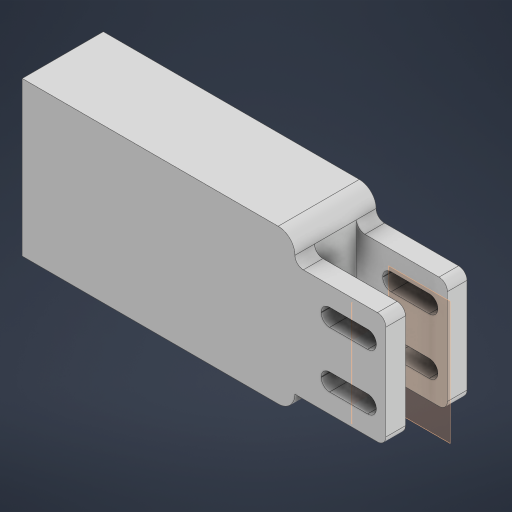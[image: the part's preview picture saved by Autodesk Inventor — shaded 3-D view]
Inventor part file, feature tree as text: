
AUTODESK INVENTOR PART (.ipt)
format: ipt  version: 2024 (Build 280153000, 153)  size: 675,840 bytes
history: native  units: mm
features: move_body x6, extrude x5, direct_edit x5, sketch x5, projected_geometry x5, fillet x4, plane x2, other x2, mirror x1, reference x1
ambient origin geometry x8: Origin, YZ Plane, XZ Plane, XY Plane, X Axis, Y Axis, Z Axis, Center Point
bodies: Solid1 (feature_tree)
feature tree (36):
  extrude  "Extrusion1"  Depth=20.0mm TaperAngle=0.0deg
  fillet  "Fillet1"  Radius=20.0mm
  plane  "Work Plane1"
  mirror  "Mirror1"
  fillet  "Fillet2"  [1 undecoded]
  extrude  "Extrusion2"  Depth=20.0mm
  fillet  "Fillet3"  Radius=10.0mm
  direct_edit  "Direct Edit1"
  extrude  "Extrusion3"  Depth=0.3mm
  direct_edit  "Direct Edit2"
  direct_edit  "Direct Edit3"
  direct_edit  "Direct Edit4"
  direct_edit  "Direct Edit5"
  extrude  "Extrusion4"  Depth=1.5mm
  fillet  "Fillet4"  Radius=1.5mm
  plane  "Work Plane2"
  extrude  "Extrusion6"  Depth=20.0mm
  sketch  "Sketch2"  dims[d0=40.0mm d1=4.0mm d2=0.0mm d5=20.0mm d6=0.0mm]
  reference  "Reference1"
  sketch  "Sketch3"  dims[d7=10.0mm d8=20.0mm d9=10.0mm]
  sketch  "Sketch4"  dims[d10=0.3mm d11=0.3mm]
  projected_geometry  "Projected Loop1"
  projected_geometry  "Projected Loop2"
  projected_geometry  "Projected Loop3"
  sketch  "Sketch5"  dims[d12=0.3mm d13=0.3mm d14=1.5mm]
  projected_geometry  "Projected Loop4"
  sketch  "Sketch7"  dims[d15=1.5mm d16=20.0mm d17=4.0mm d18=0.0mm d19=1.5mm d20=0.0mm d21=0.0mm d22=-0.5mm d23=3.0mm d24=0.0mm d25=0.0mm d26=0.0mm d27=-0.5mm d28=0.0mm d29=0.0mm d30=-0.5mm d31=0.0mm d32=0.0mm d33=-0.5mm d34=2.0mm d35=0.0mm d36=0.0mm d37=-0.5mm d38=0.0mm d39=0.0mm d40=2.0mm d41=25.25mm d42=0.0mm d43=8.0mm d44=3.0mm d50=-6.0mm d51=26.75mm d52=0.0mm]
  projected_geometry  "Projected Loop6"
  other  "Assembly1"
  other  "micro-switch:1"
  move_body  "Move1"
  move_body  "Move2"
  move_body  "Move3"
  move_body  "Move4"
  move_body  "Move5"
  move_body  "Move6"
note: 1 required parameter value undecoded (feature->parameter linkage not recoverable at this tier; creation-order binding heuristic only, values carry confidence <= 0.55)
